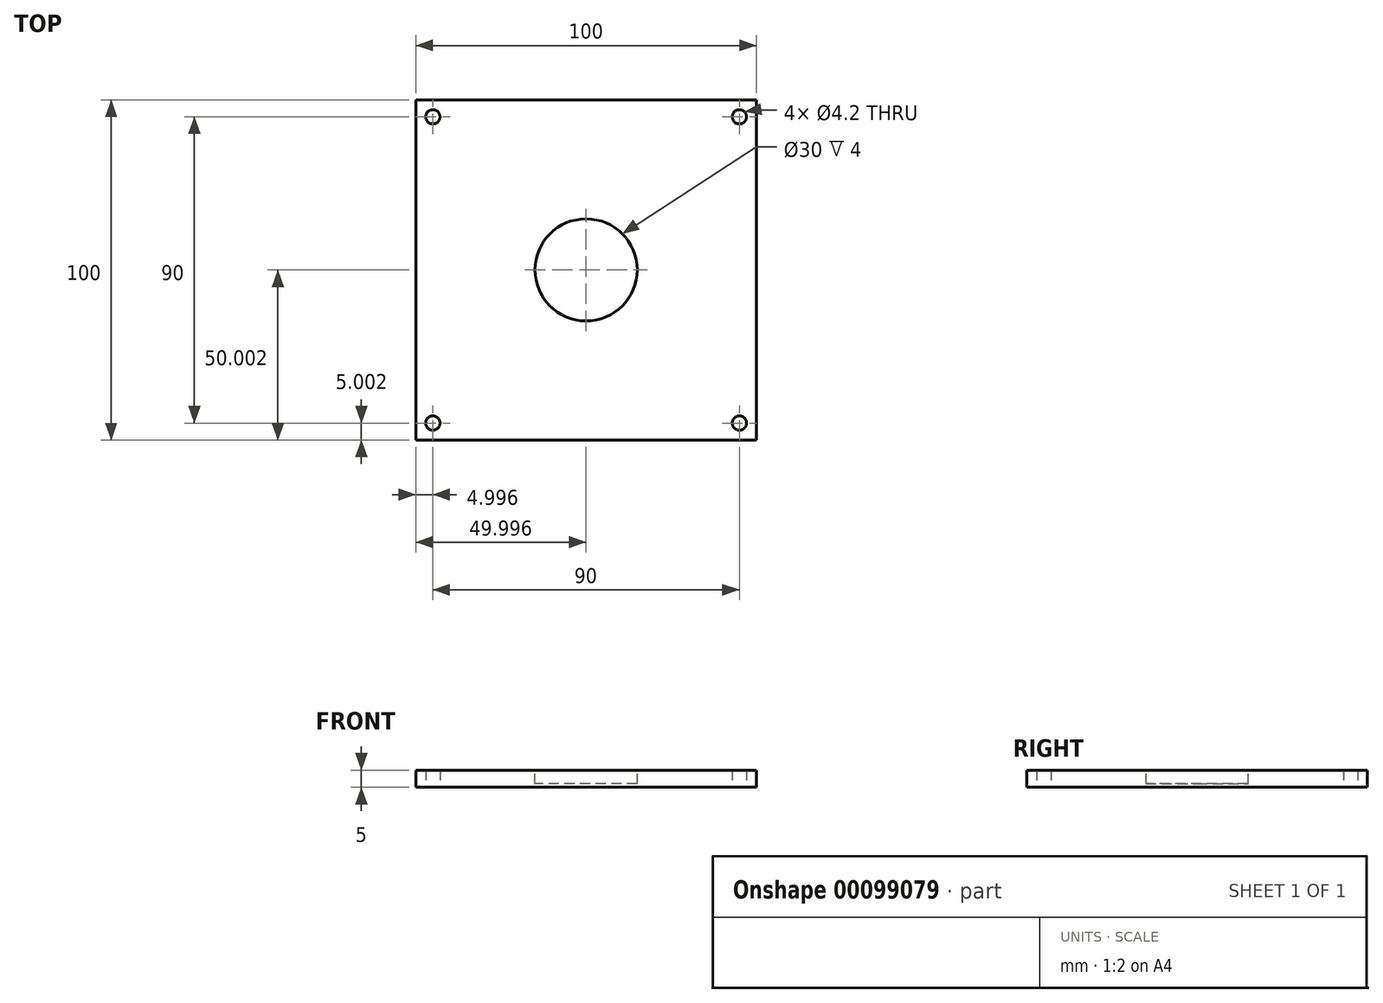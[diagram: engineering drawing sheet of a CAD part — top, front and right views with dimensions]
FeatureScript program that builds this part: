
annotation { "Feature Type Name" : "Feature", "Feature Type Description" : "" }
export const myFeature = defineFeature(function(context is Context, id is Id, definition is map)
    precondition{}
    {
        {
            var Q0;
            Q0=qCreatedBy(makeId("Top.planeOp"),FACE);
            var sketch = newSketch(context, id + "F0", { "sketchPlane" : qUnion([Q0])});
            skLineSegment(sketch, "E0.bottom", {"start": v(-46.2, -39.4) * mm, "end": v(53.8, -39.4) * mm});
            skLineSegment(sketch, "E0.top", {"start": v(-46.2, 60.6) * mm, "end": v(53.8, 60.6) * mm});
            skLineSegment(sketch, "E0.left", {"start": v(-46.2, -39.4) * mm, "end": v(-46.2, 60.6) * mm});
            skLineSegment(sketch, "E0.right", {"start": v(53.8, -39.4) * mm, "end": v(53.8, 60.6) * mm});
            skCircle(sketch, "E1", {"center": v(-41.2, 55.6) * mm, "radius": 2.1 * mm});
            skCircle(sketch, "E2", {"center": v(-41.2, -34.4) * mm, "radius": 2.1 * mm});
            skCircle(sketch, "E3", {"center": v(48.8, 55.6) * mm, "radius": 2.1 * mm});
            skCircle(sketch, "E4", {"center": v(48.8, -34.4) * mm, "radius": 2.1 * mm});
            skSolve(sketch);
        }
        {
            var Q0;
            Q0=makeQuery(id+"F0.imprint","IMPRINT",FACE,{"disambiguationData":[TD([[makeQuery(id+"F0.imprint","IMPRINT",EDGE,{"derivedFrom":sQuery(id+"F0.wireOp",EDGE,"E0.bottom")}),1.0]])]});
            extrude(context, id + "F1", {"entities" : qUnion([Q0]), "depth" : 5 * mm});
        }
        {
            var Q0;
            Q0=makeQuery(id+"F1.opExtrude","CAP_FACE",FACE,{"disambiguationData":[OSD([sQuery(id+"F0.wireOp",EDGE,"E0.bottom"),sQuery(id+"F0.wireOp",EDGE,"E0.top"),sQuery(id+"F0.wireOp",EDGE,"E0.left"),sQuery(id+"F0.wireOp",EDGE,"E0.right"),sQuery(id+"F0.wireOp",EDGE,"E1"),sQuery(id+"F0.wireOp",EDGE,"E2"),sQuery(id+"F0.wireOp",EDGE,"E3"),sQuery(id+"F0.wireOp",EDGE,"E4")])],"isStart":false});
            var sketch = newSketch(context, id + "F2", { "sketchPlane" : qUnion([Q0])});
            skCircle(sketch, "E5", {"center": v(3.8, 10.6) * mm, "radius": 15 * mm});
            skCircle(sketch, "E6", {"center": v(-21.2, 35.6) * mm, "radius": 15.2 * mm});
            skSolve(sketch);
        }
        {
            var Q0;
            Q0=makeQuery(id+"F2.imprint","IMPRINT",FACE,{"disambiguationData":[TD([[makeQuery(id+"F2.imprint","IMPRINT",EDGE,{"derivedFrom":sQuery(id+"F2.wireOp",EDGE,"E5")}),1.0]])]});
            extrude(context, id + "F3", {"entities" : qUnion([Q0]), "operationType" : NewBodyOperationType.REMOVE, "oppositeDirection" : true, "depth" : 4 * mm});
        }
    });
